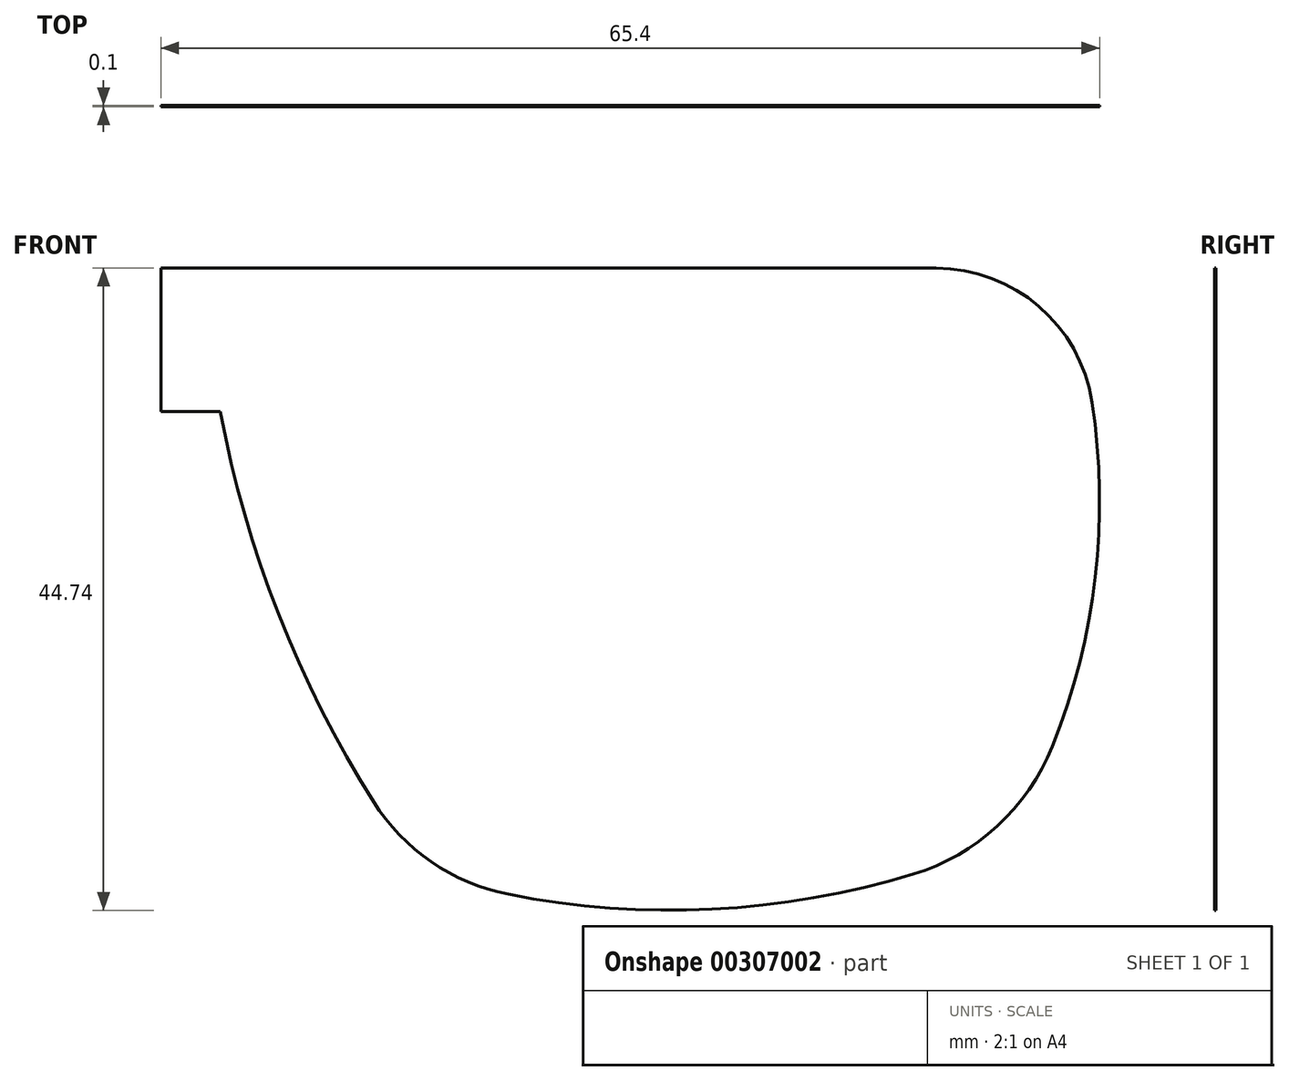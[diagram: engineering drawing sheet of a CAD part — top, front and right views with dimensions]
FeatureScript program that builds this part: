
annotation { "Feature Type Name" : "Feature", "Feature Type Description" : "" }
export const myFeature = defineFeature(function(context is Context, id is Id, definition is map)
    precondition{}
    {
        {
            var Q0;
            Q0=qCreatedBy(makeId("Front.planeOp"),FACE);
            var sketch = newSketch(context, id + "F0", { "sketchPlane" : qUnion([Q0])});
            skLineSegment(sketch, "E0", {"start": v(0, 0) * mm, "end": v(0, -14) * mm, "construction": true});
            skLineSegment(sketch, "E1.MirrorCS", {"start": v(4.5, -14) * mm, "end": v(0, -14) * mm, "construction": true});
            skArc(sketch, "E2.MirrorCS", {"start": v(68.85, -11.04) * mm, "mid": v(69.09, -23.75) * mm, "end": v(65.97, -36.07) * mm, "construction": true});
            skLineSegment(sketch, "E3.MirrorCS", {"start": v(0, 0) * mm, "end": v(56, 0) * mm, "construction": true});
            skArc(sketch, "E4.MirrorCS", {"start": v(56, 0) * mm, "mid": v(64.47, -3.14) * mm, "end": v(68.85, -11.04) * mm, "construction": true});
            skArc(sketch, "E5.MirrorCS", {"start": v(15.13, -40.25) * mm, "mid": v(8.64, -27.6) * mm, "end": v(4.5, -14) * mm, "construction": true});
            skArc(sketch, "E6.MirrorCS", {"start": v(65.97, -36.07) * mm, "mid": v(61.63, -42.35) * mm, "end": v(55.01, -46.13) * mm, "construction": true});
            skArc(sketch, "E7.MirrorCS", {"start": v(25.8, -47.58) * mm, "mid": v(19.7, -45.01) * mm, "end": v(15.13, -40.25) * mm, "construction": true});
            skArc(sketch, "E8.MirrorCS", {"start": v(55.01, -46.13) * mm, "mid": v(40.5, -48.67) * mm, "end": v(25.8, -47.58) * mm, "construction": true});
            skLineSegment(sketch, "E9.0", {"start": v(2, -2) * mm, "end": v(2, -12) * mm});
            skLineSegment(sketch, "E9.1", {"start": v(6.14, -12) * mm, "end": v(2, -12) * mm});
            skLineSegment(sketch, "E9.2", {"start": v(2, -2) * mm, "end": v(56, -2) * mm});
            skArc(sketch, "E9.3", {"start": v(16.82, -39.18) * mm, "mid": v(10.2, -26.1) * mm, "end": v(6.14, -12) * mm});
            skArc(sketch, "E9.4", {"start": v(26.19, -45.62) * mm, "mid": v(20.84, -43.37) * mm, "end": v(16.82, -39.18) * mm});
            skArc(sketch, "E9.5", {"start": v(56, -2) * mm, "mid": v(63.17, -4.66) * mm, "end": v(66.87, -11.34) * mm});
            skArc(sketch, "E9.6", {"start": v(66.87, -11.34) * mm, "mid": v(67.1, -23.52) * mm, "end": v(64.11, -35.33) * mm});
            skArc(sketch, "E9.7", {"start": v(64.11, -35.33) * mm, "mid": v(60.28, -40.88) * mm, "end": v(54.43, -44.22) * mm});
            skArc(sketch, "E9.8", {"start": v(54.43, -44.22) * mm, "mid": v(40.4, -46.67) * mm, "end": v(26.19, -45.62) * mm});
            skSolve(sketch);
        }
        {
            var Q0;
            Q0=makeQuery(id+"F0.imprint","IMPRINT",FACE,{"disambiguationData":[TD([[makeQuery(id+"F0.imprint","IMPRINT",EDGE,{"derivedFrom":sQuery(id+"F0.wireOp",EDGE,"E9.0")}),1.0]])]});
            extrude(context, id + "F1", {"entities" : qUnion([Q0]), "oppositeDirection" : true, "depth" : 0.1 * mm});
        }
    });
